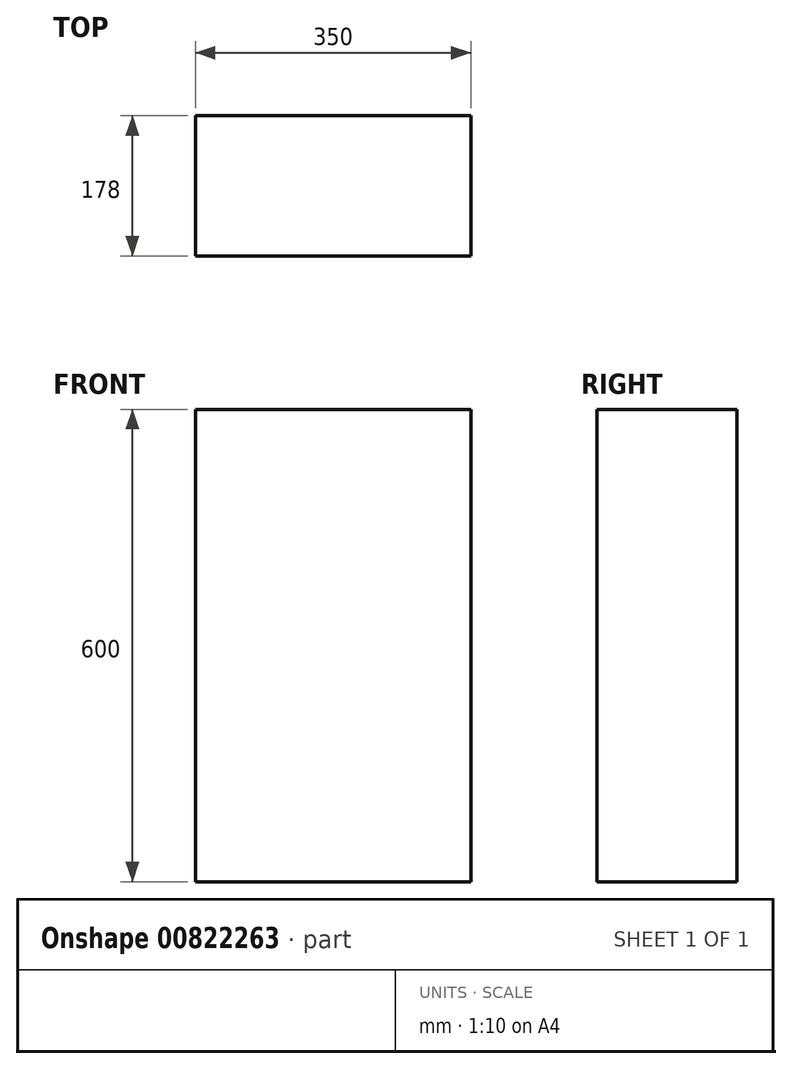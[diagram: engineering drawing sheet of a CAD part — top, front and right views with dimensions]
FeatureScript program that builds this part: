
annotation { "Feature Type Name" : "Feature", "Feature Type Description" : "" }
export const myFeature = defineFeature(function(context is Context, id is Id, definition is map)
    precondition{}
    {
        {
            var Q0;
            Q0=qCreatedBy(makeId("Front.planeOp"),FACE);
            var sketch = newSketch(context, id + "F0", { "sketchPlane" : qUnion([Q0])});
            skLineSegment(sketch, "E0.bottom", {"start": v(0, 0) * mm, "end": v(350, 0) * mm});
            skLineSegment(sketch, "E0.top", {"start": v(0, 600) * mm, "end": v(350, 600) * mm});
            skLineSegment(sketch, "E0.left", {"start": v(0, 0) * mm, "end": v(0, 600) * mm});
            skLineSegment(sketch, "E0.right", {"start": v(350, 0) * mm, "end": v(350, 600) * mm});
            skSolve(sketch);
        }
        {
            var Q0;
            Q0=makeQuery(id+"F0.imprint","IMPRINT",FACE,{"disambiguationData":[TD([[makeQuery(id+"F0.imprint","IMPRINT",EDGE,{"derivedFrom":sQuery(id+"F0.wireOp",EDGE,"E0.bottom")}),1.0]])]});
            extrude(context, id + "F1", {"entities" : qUnion([Q0]), "depth" : 178 * mm, "offsetDistance" : 25 * mm});
        }
    });
